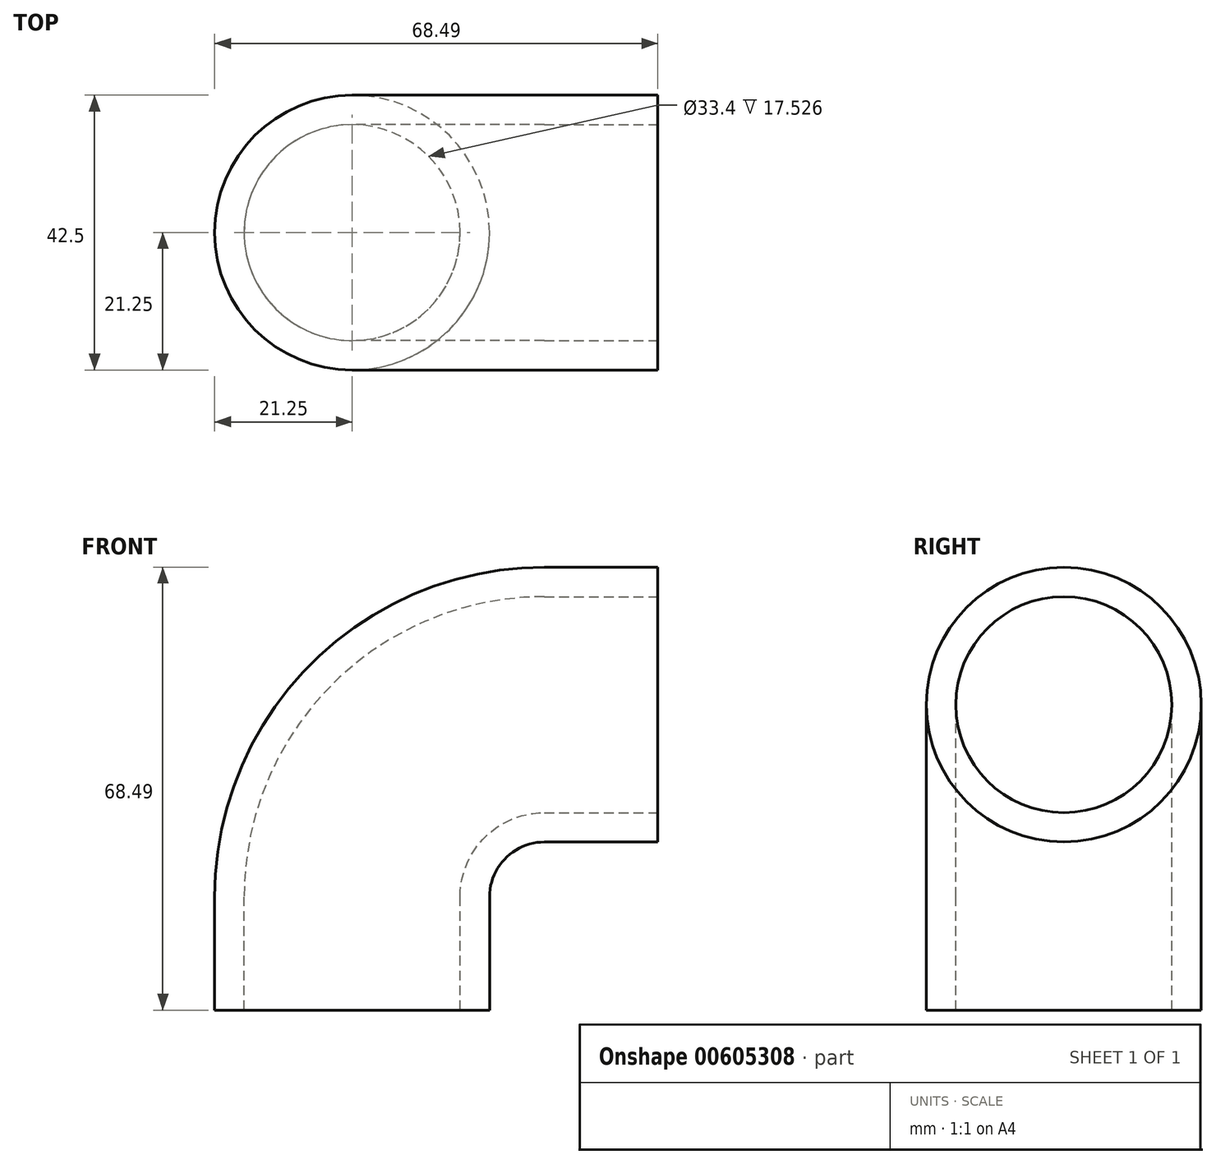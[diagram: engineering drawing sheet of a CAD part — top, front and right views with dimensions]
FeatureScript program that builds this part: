
annotation { "Feature Type Name" : "Feature", "Feature Type Description" : "" }
export const myFeature = defineFeature(function(context is Context, id is Id, definition is map)
    precondition{}
    {
        {
            var Q0;
            Q0=qCreatedBy(makeId("Top.planeOp"),FACE);
            var sketch = newSketch(context, id + "F0", { "sketchPlane" : qUnion([Q0])});
            skCircle(sketch, "E0", {"center": v(0, 0) * mm, "radius": 16.7 * mm});
            skCircle(sketch, "E1.0", {"center": v(0, 0) * mm, "radius": 21.25 * mm});
            skSolve(sketch);
        }
        {
            var Q0;
            Q0=qCreatedBy(makeId("Front.planeOp"),FACE);
            var sketch = newSketch(context, id + "F1", { "sketchPlane" : qUnion([Q0])});
            skLineSegment(sketch, "E2", {"start": v(0, 0) * mm, "end": v(0, 17.53) * mm});
            skLineSegment(sketch, "E3", {"start": v(29.72, 47.24) * mm, "end": v(47.24, 47.24) * mm});
            skPoint(sketch, "E4.visualSharp", {"position": v(0, 47.24) * mm});
            skArc(sketch, "E4.filletArc", {"start": v(29.72, 47.24) * mm, "mid": v(8.7, 38.54) * mm, "end": v(0, 17.53) * mm});
            skSolve(sketch);
        }
        {
            var Q0;
            Q0=qSketchRegion(id+"F0",true);
            var Q1;
            Q1=qConstructionFilter(qBodyType(qCreatedBy(id+"F1",EDGE),BodyType.WIRE),ConstructionObject.NO);
            sweep(context, id + "F2", {"profiles" : qUnion([Q0]), "path" : qUnion([Q1])});
        }
    });
